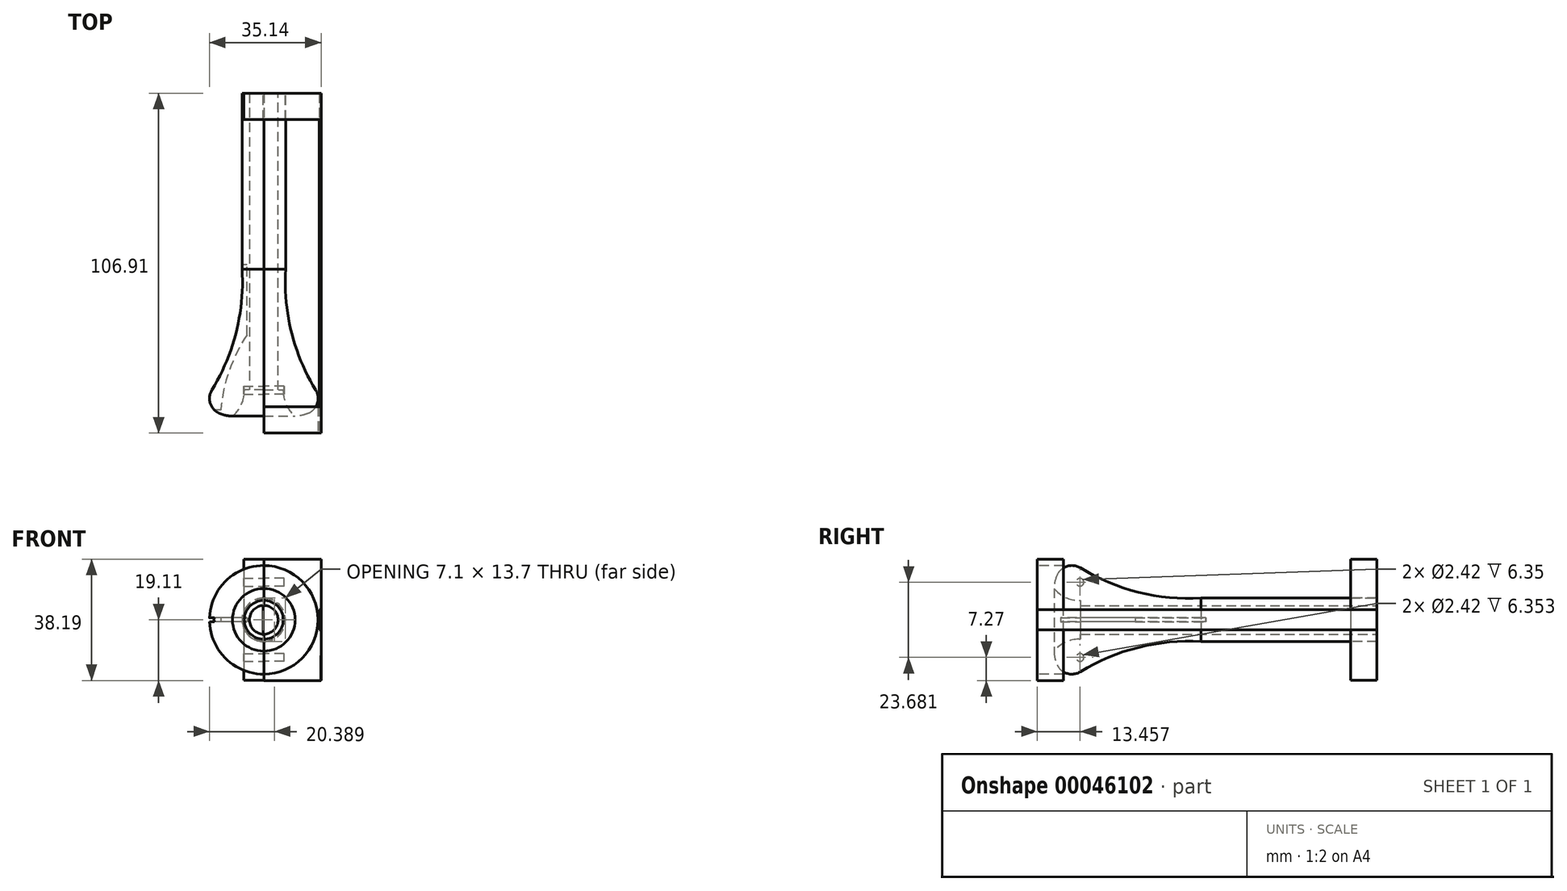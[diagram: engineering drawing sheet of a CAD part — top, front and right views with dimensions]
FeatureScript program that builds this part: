
annotation { "Feature Type Name" : "Feature", "Feature Type Description" : "" }
export const myFeature = defineFeature(function(context is Context, id is Id, definition is map)
    precondition{}
    {
        {
            var Q0;
            Q0=qCreatedBy(makeId("Right.planeOp"),FACE);
            var sketch = newSketch(context, id + "F0", { "sketchPlane" : qUnion([Q0])});
            skLineSegment(sketch, "E0", {"start": v(80.25, 0) * mm, "end": v(-33.83, 0) * mm});
            skPoint(sketch, "E1.start.orphan", {"position": v(-31.71, -1.81) * mm});
            skLineSegment(sketch, "E2", {"start": v(-31.71, -6.11) * mm, "end": v(-23.46, -6.11) * mm});
            skLineSegment(sketch, "E3", {"start": v(-23.46, -6.11) * mm, "end": v(-23.46, -4.51) * mm});
            skLineSegment(sketch, "E4", {"start": v(-23.46, -4.51) * mm, "end": v(69.89, -4.51) * mm});
            skLineSegment(sketch, "E5", {"start": v(69.89, -6.85) * mm, "end": v(14.54, -6.85) * mm});
            skLineSegment(sketch, "E6", {"start": v(69.89, -4.51) * mm, "end": v(69.89, -6.85) * mm});
            skArc(sketch, "E7", {"start": v(14.54, -6.85) * mm, "mid": v(-7.13, -9.19) * mm, "end": v(-26.82, -18.53) * mm});
            skLineSegment(sketch, "E8", {"start": v(-31.71, -6.11) * mm, "end": v(-31.71, -18.53) * mm});
            skLineSegment(sketch, "E9", {"start": v(-31.71, -18.53) * mm, "end": v(-26.82, -18.53) * mm});
            skSolve(sketch);
        }
        {
            var Q0;
            Q0 = qSketchRegion(id + "F0", true);
            var Q1;
            Q1=sQuery(id+"F0.wireOp",EDGE,"E0");
            revolve(context, id + "F1", {"entities" : qUnion([Q0]), "axis" : qUnion([Q1]), "revolveType" : RevolveType.ONE_DIRECTION, "angle" : 180 * degree});
        }
        {
            var Q0;
            Q0=makeQuery(id+"F0.imprint","IMPRINT",FACE,{"disambiguationData":[TD([[makeQuery(id+"F0.imprint","IMPRINT",EDGE,{"derivedFrom":sQuery(id+"F0.wireOp",EDGE,"E2")}),-1.0]])]});
            var Q1;
            Q1=sQuery(id+"F0.wireOp",EDGE,"E0");
            revolve(context, id + "F2", {"entities" : qUnion([Q0]), "axis" : qUnion([Q1]), "revolveType" : RevolveType.ONE_DIRECTION, "oppositeDirection" : true, "angle" : 180 * degree});
        }
        {
            var Q0;
            Q0=makeQuery(id+"F1.opRevolve","SWEPT_EDGE",EDGE,{"disambiguationData":[OSD([sQuery(id+"F0.wireOp",EDGE,"E8"),sQuery(id+"F0.wireOp",EDGE,"E9")])]});
            var Q1;
            Q1=makeQuery(id+"F2.opRevolve","SWEPT_EDGE",EDGE,{"disambiguationData":[OSD([sQuery(id+"F0.wireOp",EDGE,"E8"),sQuery(id+"F0.wireOp",EDGE,"E9")])]});
            fillet(context, id + "F3", {"entities" : qUnion([Q0, Q1]), "radius" : 10.16 * mm, "tangentPropagation" : true, "defaultsChanged" : false, "vertexSettings" : [], "allowEdgeOverflow" : false});
        }
        {
            var Q0;
            Q0=makeQuery(id+"F2.opRevolve","SWEPT_EDGE",EDGE,{"disambiguationData":[OSD([sQuery(id+"F0.wireOp",EDGE,"E7"),sQuery(id+"F0.wireOp",EDGE,"E9")])]});
            var Q1;
            Q1=makeQuery(id+"F1.opRevolve","SWEPT_EDGE",EDGE,{"disambiguationData":[OSD([sQuery(id+"F0.wireOp",EDGE,"E7"),sQuery(id+"F0.wireOp",EDGE,"E9")])]});
            var Q2;
            Q2=makeQuery(id+"F3.opFillet","BLEND_EDGE",EDGE,{"blendedFrom":[makeQuery(id+"F1.opRevolve","SWEPT_EDGE",EDGE,{"disambiguationData":[OSD([sQuery(id+"F0.wireOp",EDGE,"E8"),sQuery(id+"F0.wireOp",EDGE,"E9")])]}),makeQuery(id+"F1.opRevolve","SWEPT_FACE",FACE,{"disambiguationData":[OSD([sQuery(id+"F0.wireOp",EDGE,"E7")])]})],"blendedInto":[makeQuery(id+"F1.opRevolve","SWEPT_FACE",FACE,{"disambiguationData":[OSD([sQuery(id+"F0.wireOp",EDGE,"E7")])]})]});
            var Q3;
            Q3=makeQuery(id+"F3.opFillet","BLEND_EDGE",EDGE,{"blendedFrom":[makeQuery(id+"F2.opRevolve","SWEPT_EDGE",EDGE,{"disambiguationData":[OSD([sQuery(id+"F0.wireOp",EDGE,"E8"),sQuery(id+"F0.wireOp",EDGE,"E9")])]}),makeQuery(id+"F2.opRevolve","SWEPT_FACE",FACE,{"disambiguationData":[OSD([sQuery(id+"F0.wireOp",EDGE,"E7")])]})],"blendedInto":[makeQuery(id+"F2.opRevolve","SWEPT_FACE",FACE,{"disambiguationData":[OSD([sQuery(id+"F0.wireOp",EDGE,"E7")])]})]});
            fillet(context, id + "F4", {"entities" : qUnion([Q0, Q1, Q2, Q3]), "radius" : 5.08 * mm, "tangentPropagation" : true, "defaultsChanged" : false, "vertexSettings" : [], "allowEdgeOverflow" : false});
        }
        {
            var Q0;
            Q0=makeQuery(id+"F2.opRevolve","SWEPT_EDGE",EDGE,{"disambiguationData":[OSD([sQuery(id+"F0.wireOp",EDGE,"E2"),sQuery(id+"F0.wireOp",EDGE,"E8")])]});
            var Q1;
            Q1=makeQuery(id+"F1.opRevolve","SWEPT_EDGE",EDGE,{"disambiguationData":[OSD([sQuery(id+"F0.wireOp",EDGE,"E2"),sQuery(id+"F0.wireOp",EDGE,"E8")])]});
            fillet(context, id + "F5", {"entities" : qUnion([Q0, Q1]), "radius" : 10.16 * mm, "tangentPropagation" : true, "defaultsChanged" : false, "vertexSettings" : [], "allowEdgeOverflow" : false});
        }
        {
            var Q0;
            Q0=qCreatedBy(makeId("Top.planeOp"),FACE);
            var sketch = newSketch(context, id + "F6", { "sketchPlane" : qUnion([Q0])});
            skLineSegment(sketch, "E10", {"start": v(-13.55, -29.73) * mm, "end": v(-19.43, -29.73) * mm});
            skLineSegment(sketch, "E11", {"start": v(-19.43, -29.73) * mm, "end": v(-19.43, 16.07) * mm});
            skLineSegment(sketch, "E12", {"start": v(-19.43, 16.07) * mm, "end": v(-5.3, 16.07) * mm});
            skLineSegment(sketch, "E13", {"start": v(-5.3, -6.16) * mm, "end": v(-5.3, 16.07) * mm});
            skArc(sketch, "E14", {"start": v(-5.3, -6.16) * mm, "mid": v(-10.89, -17.43) * mm, "end": v(-13.55, -29.73) * mm});
            skSolve(sketch);
        }
        {
            var Q0;
            Q0 = qSketchRegion(id + "F6", true);
            extrude(context, id + "F7", {"entities" : qUnion([Q0]), "operationType" : NewBodyOperationType.REMOVE, "depth" : 1.27 * mm, "symmetric" : true});
        }
        {
            var Q0;
            Q0=qCreatedBy(makeId("Right.planeOp"),FACE);
            var sketch = newSketch(context, id + "F8", { "sketchPlane" : qUnion([Q0])});
            skCircle(sketch, "E15", {"center": v(-23.56, 11.84) * mm, "radius": 1.21 * mm});
            skCircle(sketch, "E16.MirrorC", {"center": v(-23.56, -11.84) * mm, "radius": 1.21 * mm});
            skSolve(sketch);
        }
        {
            var Q0;
            Q0 = qSketchRegion(id + "F8", true);
            extrude(context, id + "F9", {"entities" : qUnion([Q0]), "operationType" : NewBodyOperationType.REMOVE, "depth" : 6.35 * mm});
        }
        {
            var Q0;
            Q0 = qSketchRegion(id + "F8", true);
            extrude(context, id + "F10", {"entities" : qUnion([Q0]), "operationType" : NewBodyOperationType.REMOVE, "oppositeDirection" : true, "depth" : 6.35 * mm});
        }
        {
            var Q0;
            Q0=makeQuery(id+"F1.opRevolve","SWEPT_FACE",FACE,{"disambiguationData":[OSD([sQuery(id+"F0.wireOp",EDGE,"E6")])]});
            var sketch = newSketch(context, id + "F11", { "sketchPlane" : qUnion([Q0])});
            skArc(sketch, "E17", {"start": v(0, 6.85) * mm, "mid": v(-6.85, 0) * mm, "end": v(0, -6.85) * mm});
            skLineSegment(sketch, "E18", {"start": v(0, 19.04) * mm, "end": v(-18.05, 19.04) * mm});
            skLineSegment(sketch, "E19", {"start": v(-18.05, 19.04) * mm, "end": v(-18.05, 0) * mm});
            skLineSegment(sketch, "E20.MirrorCS", {"start": v(0, -19.04) * mm, "end": v(-18.05, -19.04) * mm});
            skLineSegment(sketch, "E21.MirrorCS", {"start": v(-18.05, -19.04) * mm, "end": v(-18.05, 0) * mm});
            skLineSegment(sketch, "E22", {"start": v(0, 19.04) * mm, "end": v(6.33, 19.04) * mm});
            skLineSegment(sketch, "E23", {"start": v(6.33, 19.04) * mm, "end": v(6.33, -19.04) * mm});
            skLineSegment(sketch, "E24", {"start": v(6.33, -19.04) * mm, "end": v(0, -19.04) * mm});
            skLineSegment(sketch, "E25", {"start": v(0, 6.85) * mm, "end": v(0.25, 6.85) * mm});
            skLineSegment(sketch, "E26", {"start": v(0.25, 6.85) * mm, "end": v(0.25, -6.85) * mm});
            skLineSegment(sketch, "E27", {"start": v(0.25, -6.85) * mm, "end": v(0, -6.85) * mm});
            skSolve(sketch);
        }
        {
            var Q0;
            Q0 = qSketchRegion(id + "F11", true);
            extrude(context, id + "F12", {"entities" : qUnion([Q0]), "oppositeDirection" : true, "depth" : 8.25 * mm});
        }
        {
            var Q0;
            Q0=makeQuery(id+"F12.opExtrude","SWEPT_FACE",FACE,{"disambiguationData":[OSD([sQuery(id+"F11.wireOp",EDGE,"E19"),sQuery(id+"F11.wireOp",EDGE,"E21.MirrorCS")])]});
            var sketch = newSketch(context, id + "F13", { "sketchPlane" : qUnion([Q0])});
            skLineSegment(sketch, "E28", {"start": v(69.89, 3.2) * mm, "end": v(-37.02, 3.2) * mm});
            skLineSegment(sketch, "E29.MirrorCS", {"start": v(69.89, -3.2) * mm, "end": v(-37.02, -3.2) * mm});
            skLineSegment(sketch, "E30", {"start": v(69.89, -3.2) * mm, "end": v(69.89, 3.2) * mm});
            skLineSegment(sketch, "E31", {"start": v(-37.02, -3.2) * mm, "end": v(-37.02, 3.2) * mm});
            skLineSegment(sketch, "E32", {"start": v(61.63, -3.2) * mm, "end": v(61.63, 3.2) * mm});
            skSolve(sketch);
        }
        {
            var Q0;
            {var subQ0=sQuery(id+"F13.wireOp",EDGE,"E30");Q0=makeQuery(id+"F13.imprint","IMPRINT",FACE,{"disambiguationData":[TD([[makeQuery(id+"F13.imprint","IMPRINT",EDGE,{"derivedFrom":subQ0}),-1.0]])]});}
            extrude(context, id + "F14", {"entities" : qUnion([Q0]), "operationType" : NewBodyOperationType.REMOVE, "oppositeDirection" : true, "depth" : 0.64 * mm});
        }
        {
            var Q0;
            {var subQ0=sQuery(id+"F13.wireOp",EDGE,"E30");Q0=makeQuery(id+"F13.imprint","IMPRINT",FACE,{"disambiguationData":[TD([[makeQuery(id+"F13.imprint","IMPRINT",EDGE,{"derivedFrom":subQ0}),-1.0]])]});}
            var Q1;
            {var subQ0=sQuery(id+"F13.wireOp",EDGE,"E31");Q1=makeQuery(id+"F13.imprint","IMPRINT",FACE,{"disambiguationData":[TD([[makeQuery(id+"F13.imprint","IMPRINT",EDGE,{"derivedFrom":subQ0}),-1.0]])]});}
            extrude(context, id + "F15", {"entities" : qUnion([Q0, Q1]), "oppositeDirection" : true, "depth" : 0.64 * mm});
        }
        {
            var Q0;
            Q0=makeQuery(id+"F15.opExtrude","SWEPT_FACE",FACE,{"disambiguationData":[OSD([sQuery(id+"F13.wireOp",EDGE,"E31")])]});
            var sketch = newSketch(context, id + "F16", { "sketchPlane" : qUnion([Q0])});
            skLineSegment(sketch, "E33", {"start": v(0, -19.11) * mm, "end": v(17.96, -19.11) * mm});
            skLineSegment(sketch, "E34", {"start": v(17.96, -19.11) * mm, "end": v(18.05, -3.2) * mm});
            skLineSegment(sketch, "E35", {"start": v(18.05, -3.2) * mm, "end": v(17.42, -3.2) * mm});
            skLineSegment(sketch, "E36", {"start": v(17.42, -3.2) * mm, "end": v(17.42, 3.2) * mm});
            skLineSegment(sketch, "E37", {"start": v(17.42, 3.2) * mm, "end": v(18.05, 3.2) * mm});
            skLineSegment(sketch, "E38", {"start": v(18.05, 3.2) * mm, "end": v(18.05, 19.08) * mm});
            skLineSegment(sketch, "E39", {"start": v(18.05, 19.08) * mm, "end": v(0, 19.08) * mm});
            skLineSegment(sketch, "E40", {"start": v(0, -19.11) * mm, "end": v(0, -17.08) * mm});
            skArc(sketch, "E41", {"start": v(0, -17.08) * mm, "mid": v(17.08, 0) * mm, "end": v(0, 17.08) * mm});
            skLineSegment(sketch, "E42", {"start": v(0, 19.08) * mm, "end": v(0, 17.08) * mm});
            skSolve(sketch);
        }
        {
            var Q0;
            Q0 = qSketchRegion(id + "F16", true);
            extrude(context, id + "F17", {"entities" : qUnion([Q0]), "oppositeDirection" : true, "depth" : 8.25 * mm});
        }
    });
